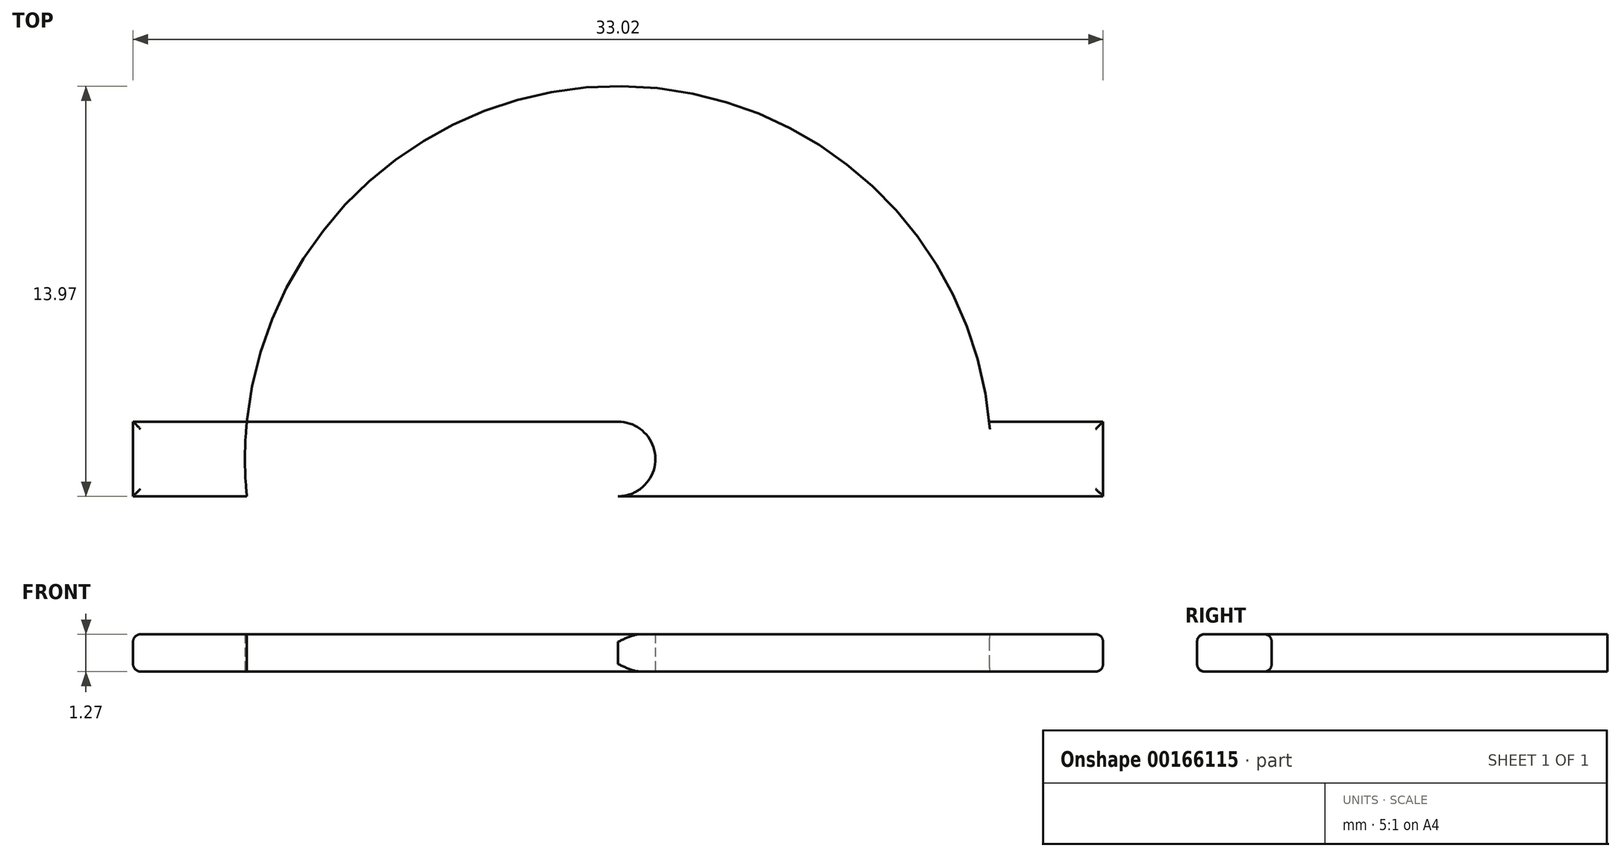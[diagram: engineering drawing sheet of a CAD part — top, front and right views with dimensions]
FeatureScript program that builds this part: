
annotation { "Feature Type Name" : "Feature", "Feature Type Description" : "" }
export const myFeature = defineFeature(function(context is Context, id is Id, definition is map)
    precondition{}
    {
        {
            var Q0;
            Q0=qCreatedBy(makeId("Top.planeOp"),FACE);
            var sketch = newSketch(context, id + "F0", { "sketchPlane" : qUnion([Q0])});
            skPoint(sketch, "E0", {"position": v(0, 0) * mm});
            skCircle(sketch, "E1", {"center": v(0, 0) * mm, "radius": 12.7 * mm});
            skPoint(sketch, "E2", {"position": v(12.7, 0) * mm});
            skPoint(sketch, "E3", {"position": v(-12.7, 0) * mm});
            skLineSegment(sketch, "E4.bottom", {"start": v(16.51, 1.27) * mm, "end": v(-16.51, 1.27) * mm});
            skLineSegment(sketch, "E4.top", {"start": v(16.51, -1.27) * mm, "end": v(-16.51, -1.27) * mm});
            skLineSegment(sketch, "E4.left", {"start": v(16.51, 1.27) * mm, "end": v(16.51, -1.27) * mm});
            skLineSegment(sketch, "E4.right", {"start": v(-16.51, 1.27) * mm, "end": v(-16.51, -1.27) * mm});
            skCircle(sketch, "E5", {"center": v(0, 0) * mm, "radius": 1.27 * mm});
            skPoint(sketch, "E6", {"position": v(0, -1.27) * mm});
            skSolve(sketch);
        }
        {
            var Q0;
            {var subQ0=sQuery(id+"F0.wireOp",EDGE,"E4.top");var subQ1=sQuery(id+"F0.wireOp",EDGE,"E1");var subQ2=makeQuery(id+"F0.imprint","INTERSECT",VERTEX,{"disambiguationData":[OD(0.0)],"derivedFrom":[subQ1,subQ0]});Q0=makeQuery(id+"F0.imprint","IMPRINT",FACE,{"disambiguationData":[TD([[makeQuery(id+"F0.imprint","IMPRINT",EDGE,{"disambiguationData":[TD([[subQ2,-1.0]])],"derivedFrom":subQ1}),1.0]])]});}
            var Q1;
            {var subQ0=sQuery(id+"F0.wireOp",EDGE,"E4.bottom");var subQ1=sQuery(id+"F0.wireOp",EDGE,"E1");var subQ2=makeQuery(id+"F0.imprint","INTERSECT",VERTEX,{"disambiguationData":[OD(0.0)],"derivedFrom":[subQ1,subQ0]});Q1=makeQuery(id+"F0.imprint","IMPRINT",FACE,{"disambiguationData":[TD([[makeQuery(id+"F0.imprint","IMPRINT",EDGE,{"disambiguationData":[TD([[subQ2,1.0]])],"derivedFrom":subQ1}),1.0]])]});}
            var Q2;
            {var subQ5=sQuery(id+"F0.wireOp",EDGE,"E4.left");Q2=makeQuery(id+"F0.imprint","IMPRINT",FACE,{"disambiguationData":[TD([[makeQuery(id+"F0.imprint","IMPRINT",EDGE,{"derivedFrom":subQ5}),-1.0]])]});}
            var Q3;
            {var subQ0=sQuery(id+"F0.wireOp",EDGE,"E4.bottom");var subQ1=sQuery(id+"F0.wireOp",EDGE,"E1");var subQ2=makeQuery(id+"F0.imprint","INTERSECT",VERTEX,{"disambiguationData":[OD(0.0)],"derivedFrom":[subQ1,subQ0]});Q3=makeQuery(id+"F0.imprint","IMPRINT",FACE,{"disambiguationData":[TD([[makeQuery(id+"F0.imprint","IMPRINT",EDGE,{"disambiguationData":[TD([[subQ2,-1.0]])],"derivedFrom":subQ1}),1.0]])]});}
            var Q4;
            {var subQ5=sQuery(id+"F0.wireOp",EDGE,"E4.right");Q4=makeQuery(id+"F0.imprint","IMPRINT",FACE,{"disambiguationData":[TD([[makeQuery(id+"F0.imprint","IMPRINT",EDGE,{"derivedFrom":subQ5}),1.0]])]});}
            var Q5;
            {var subQ0=sQuery(id+"F0.wireOp",EDGE,"E4.bottom");var subQ1=sQuery(id+"F0.wireOp",EDGE,"E1");var subQ2=makeQuery(id+"F0.imprint","INTERSECT",VERTEX,{"disambiguationData":[OD(1.0)],"derivedFrom":[subQ1,subQ0]});Q5=makeQuery(id+"F0.imprint","IMPRINT",FACE,{"disambiguationData":[TD([[makeQuery(id+"F0.imprint","IMPRINT",EDGE,{"disambiguationData":[TD([[subQ2,1.0]])],"derivedFrom":subQ1}),1.0]])]});}
            extrude(context, id + "F3", {"entities" : qUnion([Q0, Q1, Q2, Q3, Q4, Q5]), "depth" : 1.27 * mm});
        }
        {
            var Q0;
            {var subQ0=sQuery(id+"F0.wireOp",EDGE,"E4.bottom");var subQ1=sQuery(id+"F0.wireOp",EDGE,"E1");Q0=makeQuery(id+"F3.opExtrude","CAP_EDGE",EDGE,{"disambiguationData":[OSD([subQ1]),TDD([makeQuery(id+"F0.imprint","IMPRINT",EDGE,{"disambiguationData":[TD([[makeQuery(id+"F0.imprint","INTERSECT",VERTEX,{"disambiguationData":[OD(0.0)],"derivedFrom":[subQ1,subQ0]}),1.0]])],"derivedFrom":subQ1})])],"isStart":false});}
            var Q1;
            {var subQ0=sQuery(id+"F0.wireOp",EDGE,"E4.bottom");Q1=makeQuery(id+"F3.opExtrude","CAP_EDGE",EDGE,{"disambiguationData":[OSD([subQ0]),TDD([makeQuery(id+"F0.imprint","IMPRINT",EDGE,{"disambiguationData":[TD([[makeQuery(id+"F0.imprint","INTERSECT",VERTEX,{"derivedFrom":[subQ0,sQuery(id+"F0.wireOp",EDGE,"E4.right")]}),1.0]])],"derivedFrom":subQ0})])],"isStart":false});}
            var Q2;
            {var subQ0=sQuery(id+"F0.wireOp",EDGE,"E4.top");Q2=makeQuery(id+"F3.opExtrude","CAP_EDGE",EDGE,{"disambiguationData":[OSD([subQ0]),TDD([makeQuery(id+"F0.imprint","IMPRINT",EDGE,{"disambiguationData":[TD([[makeQuery(id+"F0.imprint","INTERSECT",VERTEX,{"derivedFrom":[subQ0,sQuery(id+"F0.wireOp",EDGE,"E4.right")]}),1.0]])],"derivedFrom":subQ0})])],"isStart":false});}
            var Q3;
            {var subQ0=sQuery(id+"F0.wireOp",EDGE,"E4.top");var subQ1=sQuery(id+"F0.wireOp",EDGE,"E1");Q3=makeQuery(id+"F3.opExtrude","CAP_EDGE",EDGE,{"disambiguationData":[OSD([subQ1]),TDD([makeQuery(id+"F0.imprint","IMPRINT",EDGE,{"disambiguationData":[TD([[makeQuery(id+"F0.imprint","INTERSECT",VERTEX,{"disambiguationData":[OD(0.0)],"derivedFrom":[subQ1,subQ0]}),-1.0]])],"derivedFrom":subQ1})])],"isStart":false});}
            var Q4;
            Q4=makeQuery(id+"F3.opExtrude","CAP_EDGE",EDGE,{"disambiguationData":[OSD([sQuery(id+"F0.wireOp",EDGE,"E4.right")])],"isStart":false});
            var Q5;
            {var subQ0=sQuery(id+"F0.wireOp",EDGE,"E4.bottom");Q5=makeQuery(id+"F3.opExtrude","CAP_EDGE",EDGE,{"disambiguationData":[OSD([subQ0]),TDD([makeQuery(id+"F0.imprint","IMPRINT",EDGE,{"disambiguationData":[TD([[makeQuery(id+"F0.imprint","INTERSECT",VERTEX,{"derivedFrom":[subQ0,sQuery(id+"F0.wireOp",EDGE,"E4.left")]}),-1.0]])],"derivedFrom":subQ0})])],"isStart":false});}
            var Q6;
            {var subQ0=sQuery(id+"F0.wireOp",EDGE,"E4.top");Q6=makeQuery(id+"F3.opExtrude","CAP_EDGE",EDGE,{"disambiguationData":[OSD([subQ0]),TDD([makeQuery(id+"F0.imprint","IMPRINT",EDGE,{"disambiguationData":[TD([[makeQuery(id+"F0.imprint","INTERSECT",VERTEX,{"derivedFrom":[subQ0,sQuery(id+"F0.wireOp",EDGE,"E4.left")]}),-1.0]])],"derivedFrom":subQ0})])],"isStart":false});}
            var Q7;
            Q7=makeQuery(id+"F3.opExtrude","CAP_EDGE",EDGE,{"disambiguationData":[OSD([sQuery(id+"F0.wireOp",EDGE,"E4.left")])],"isStart":false});
            fillet(context, id + "F1", {"entities" : qUnion([Q0, Q1, Q2, Q3, Q4, Q5, Q6, Q7]), "radius" : 0.25 * mm, "tangentPropagation" : true, "allowEdgeOverflow" : false});
        }
        {
            var Q0;
            {var subQ0=sQuery(id+"F0.wireOp",EDGE,"E4.top");Q0=makeQuery(id+"F3.opExtrude","CAP_EDGE",EDGE,{"disambiguationData":[OSD([subQ0]),TDD([makeQuery(id+"F0.imprint","IMPRINT",EDGE,{"disambiguationData":[TD([[makeQuery(id+"F0.imprint","INTERSECT",VERTEX,{"derivedFrom":[subQ0,sQuery(id+"F0.wireOp",EDGE,"E4.left")]}),-1.0]])],"derivedFrom":subQ0})])],"isStart":true});}
            var Q1;
            Q1=makeQuery(id+"F3.opExtrude","CAP_EDGE",EDGE,{"disambiguationData":[OSD([sQuery(id+"F0.wireOp",EDGE,"E4.left")])],"isStart":true});
            var Q2;
            {var subQ0=sQuery(id+"F0.wireOp",EDGE,"E4.bottom");Q2=makeQuery(id+"F3.opExtrude","CAP_EDGE",EDGE,{"disambiguationData":[OSD([subQ0]),TDD([makeQuery(id+"F0.imprint","IMPRINT",EDGE,{"disambiguationData":[TD([[makeQuery(id+"F0.imprint","INTERSECT",VERTEX,{"derivedFrom":[subQ0,sQuery(id+"F0.wireOp",EDGE,"E4.left")]}),-1.0]])],"derivedFrom":subQ0})])],"isStart":true});}
            var Q3;
            {var subQ0=sQuery(id+"F0.wireOp",EDGE,"E4.bottom");var subQ1=sQuery(id+"F0.wireOp",EDGE,"E1");Q3=makeQuery(id+"F3.opExtrude","CAP_EDGE",EDGE,{"disambiguationData":[OSD([subQ1]),TDD([makeQuery(id+"F0.imprint","IMPRINT",EDGE,{"disambiguationData":[TD([[makeQuery(id+"F0.imprint","INTERSECT",VERTEX,{"disambiguationData":[OD(0.0)],"derivedFrom":[subQ1,subQ0]}),1.0]])],"derivedFrom":subQ1})])],"isStart":true});}
            var Q4;
            {var subQ0=sQuery(id+"F0.wireOp",EDGE,"E4.bottom");Q4=makeQuery(id+"F3.opExtrude","CAP_EDGE",EDGE,{"disambiguationData":[OSD([subQ0]),TDD([makeQuery(id+"F0.imprint","IMPRINT",EDGE,{"disambiguationData":[TD([[makeQuery(id+"F0.imprint","INTERSECT",VERTEX,{"derivedFrom":[subQ0,sQuery(id+"F0.wireOp",EDGE,"E4.right")]}),1.0]])],"derivedFrom":subQ0})])],"isStart":true});}
            var Q5;
            {var subQ0=sQuery(id+"F0.wireOp",EDGE,"E4.top");Q5=makeQuery(id+"F3.opExtrude","CAP_EDGE",EDGE,{"disambiguationData":[OSD([subQ0]),TDD([makeQuery(id+"F0.imprint","IMPRINT",EDGE,{"disambiguationData":[TD([[makeQuery(id+"F0.imprint","INTERSECT",VERTEX,{"derivedFrom":[subQ0,sQuery(id+"F0.wireOp",EDGE,"E4.right")]}),1.0]])],"derivedFrom":subQ0})])],"isStart":true});}
            var Q6;
            {var subQ0=sQuery(id+"F0.wireOp",EDGE,"E4.top");var subQ1=sQuery(id+"F0.wireOp",EDGE,"E1");Q6=makeQuery(id+"F3.opExtrude","CAP_EDGE",EDGE,{"disambiguationData":[OSD([subQ1]),TDD([makeQuery(id+"F0.imprint","IMPRINT",EDGE,{"disambiguationData":[TD([[makeQuery(id+"F0.imprint","INTERSECT",VERTEX,{"disambiguationData":[OD(0.0)],"derivedFrom":[subQ1,subQ0]}),-1.0]])],"derivedFrom":subQ1})])],"isStart":true});}
            var Q7;
            Q7=makeQuery(id+"F3.opExtrude","CAP_EDGE",EDGE,{"disambiguationData":[OSD([sQuery(id+"F0.wireOp",EDGE,"E4.right")])],"isStart":true});
            fillet(context, id + "F2", {"entities" : qUnion([Q0, Q1, Q2, Q3, Q4, Q5, Q6, Q7]), "radius" : 0.25 * mm, "tangentPropagation" : true, "allowEdgeOverflow" : false});
        }
    });
